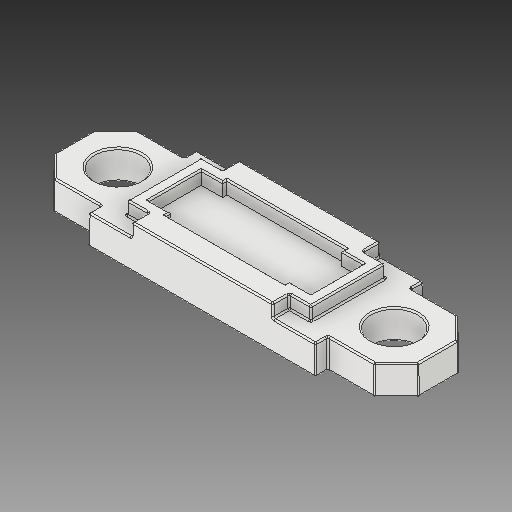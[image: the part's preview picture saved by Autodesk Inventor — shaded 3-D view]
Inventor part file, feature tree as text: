
AUTODESK INVENTOR PART (.ipt)
format: ipt  version: 2019 (Build 230136000, 136)  size: 348,160 bytes
history: native  units: in
note: dims shown in document units (in); Inventor stores cm internally (conversion verified against a paired STEP export)
features: fillet x1
ambient origin geometry x8: Origin, YZ Plane, XZ Plane, XY Plane, X Axis, Y Axis, Z Axis, Center Point
bodies: Solid1 (feature_tree)
feature tree (1):
  fillet  "Fillet1"  [1 undecoded]
note: 1 required parameter value undecoded (feature->parameter linkage not recoverable at this tier; creation-order binding heuristic only, values carry confidence <= 0.55)
